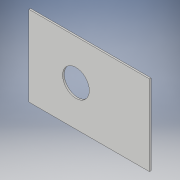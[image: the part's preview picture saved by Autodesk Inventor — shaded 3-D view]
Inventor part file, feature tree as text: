
AUTODESK INVENTOR PART (.ipt)
format: ipt  version: 2017 (Build 210142000, 142)  size: 96,768 bytes
history: native  units: in
note: dims shown in document units (in); Inventor stores cm internally (conversion verified against a paired STEP export)
features: sketch x2, extrude x1
ambient origin geometry x8: Origin, YZ Plane, XZ Plane, XY Plane, X Axis, Y Axis, Z Axis, Center Point
bodies: Solid1 (feature_tree)
feature tree (3):
  sketch  "Sketch1"  dims[d0=18.0in d1=12.0in]
  sketch  "Sketch2"  dims[d4=4.0in d5=0.25in d6=0.0in]
  extrude  "Extrusion1"  Depth=12.0in
